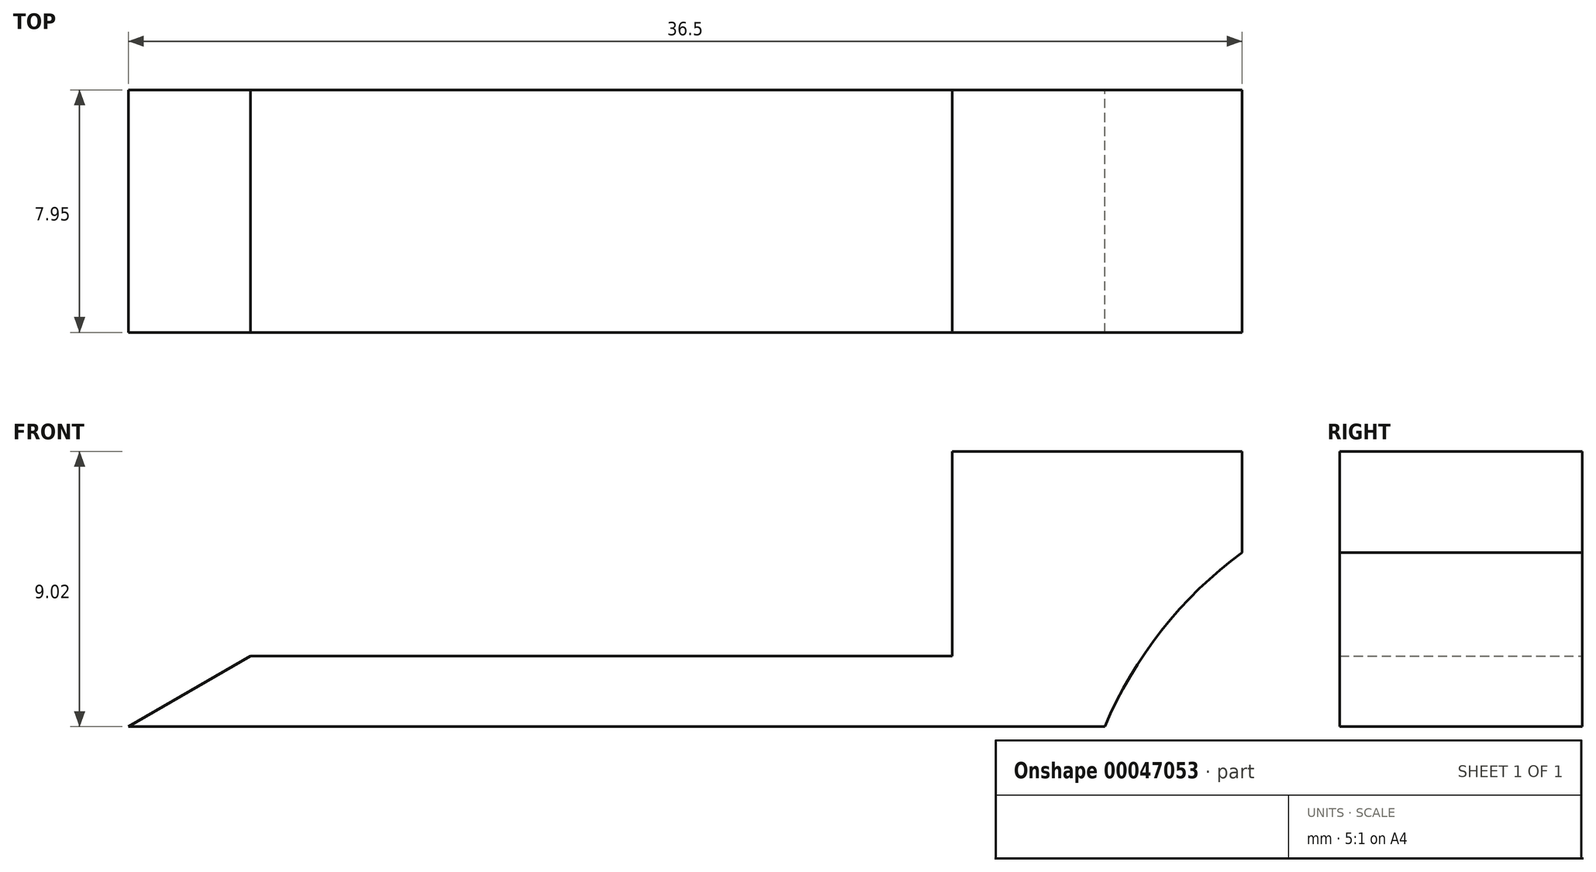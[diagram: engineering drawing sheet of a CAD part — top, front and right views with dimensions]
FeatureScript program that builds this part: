
annotation { "Feature Type Name" : "Feature", "Feature Type Description" : "" }
export const myFeature = defineFeature(function(context is Context, id is Id, definition is map)
    precondition{}
    {
        {
            var Q0;
            Q0=qCreatedBy(makeId("Front.planeOp"),FACE);
            var sketch = newSketch(context, id + "F0", { "sketchPlane" : qUnion([Q0])});
            skLineSegment(sketch, "E0", {"start": v(0, 0) * mm, "end": v(4.1, 4.1) * mm});
            skLineSegment(sketch, "E1", {"start": v(27, 9.02) * mm, "end": v(27, 9.02) * mm});
            skLineSegment(sketch, "E2", {"start": v(27, 9.02) * mm, "end": v(36.5, 9.02) * mm});
            skLineSegment(sketch, "E3", {"start": v(36.5, 9.02) * mm, "end": v(36.5, 0) * mm});
            skLineSegment(sketch, "E4", {"start": v(36.5, 0) * mm, "end": v(0, 0) * mm});
            skLineSegment(sketch, "E5", {"start": v(0, 0) * mm, "end": v(0, -0.2) * mm, "construction": true});
            skLineSegment(sketch, "E6", {"start": v(0, -0.2) * mm, "end": v(3, -0.2) * mm, "construction": true});
            skLineSegment(sketch, "E7", {"start": v(3, -0.2) * mm, "end": v(3, 0) * mm, "construction": true});
            skLineSegment(sketch, "E8", {"start": v(3, 0) * mm, "end": v(10.45, 7.45) * mm, "construction": true});
            skLineSegment(sketch, "E9", {"start": v(0, 0) * mm, "end": v(15.84, 9.14) * mm});
            skLineSegment(sketch, "E10", {"start": v(27, 4.1) * mm, "end": v(4.1, 4.1) * mm});
            skPoint(sketch, "E11", {"position": v(7.1, 4.1) * mm});
            skLineSegment(sketch, "E12", {"start": v(27, 9.02) * mm, "end": v(27, 4.1) * mm});
            skLineSegment(sketch, "E13", {"start": v(4, 2.3) * mm, "end": v(27, 2.3) * mm});
            skLineSegment(sketch, "E14", {"start": v(27, 2.3) * mm, "end": v(27, 4.1) * mm});
            skLineSegment(sketch, "E15", {"start": v(27, 0) * mm, "end": v(27, -0.2) * mm, "construction": true});
            skLineSegment(sketch, "E16", {"start": v(27, -0.2) * mm, "end": v(32, -0.2) * mm, "construction": true});
            skLineSegment(sketch, "E17", {"start": v(32, -0.2) * mm, "end": v(32, 0) * mm, "construction": true});
            skLineSegment(sketch, "E18", {"start": v(32, 0) * mm, "end": v(36.5, 7.8) * mm, "construction": true});
            skLineSegment(sketch, "E19", {"start": v(25.41, 0) * mm, "end": v(32, 0) * mm});
            skLineSegment(sketch, "E20", {"start": v(32, 0) * mm, "end": v(29.65, 8.75) * mm, "construction": true});
            skLineSegment(sketch, "E21", {"start": v(27, 2.3) * mm, "end": v(34.7, 10) * mm, "construction": true});
            skLineSegment(sketch, "E22", {"start": v(24.8, 1.23) * mm, "end": v(32.67, 1.16) * mm, "construction": true});
            skLineSegment(sketch, "E23", {"start": v(32.67, 1.16) * mm, "end": v(28.3, 10.09) * mm, "construction": true});
            skArc(sketch, "E24", {"start": v(36.5, 5.7) * mm, "mid": v(33.86, 3.16) * mm, "end": v(32, 0) * mm});
            skSolve(sketch);
        }
        {
            var Q0;
            {var subQ4=sQuery(id+"F0.wireOp",EDGE,"E2");Q0=makeQuery(id+"F0.imprint","IMPRINT",FACE,{"disambiguationData":[TD([[makeQuery(id+"F0.imprint","IMPRINT",EDGE,{"derivedFrom":subQ4}),-1.0]])]});}
            extrude(context, id + "F1", {"entities" : qUnion([Q0]), "depth" : 7.95 * mm});
        }
    });
